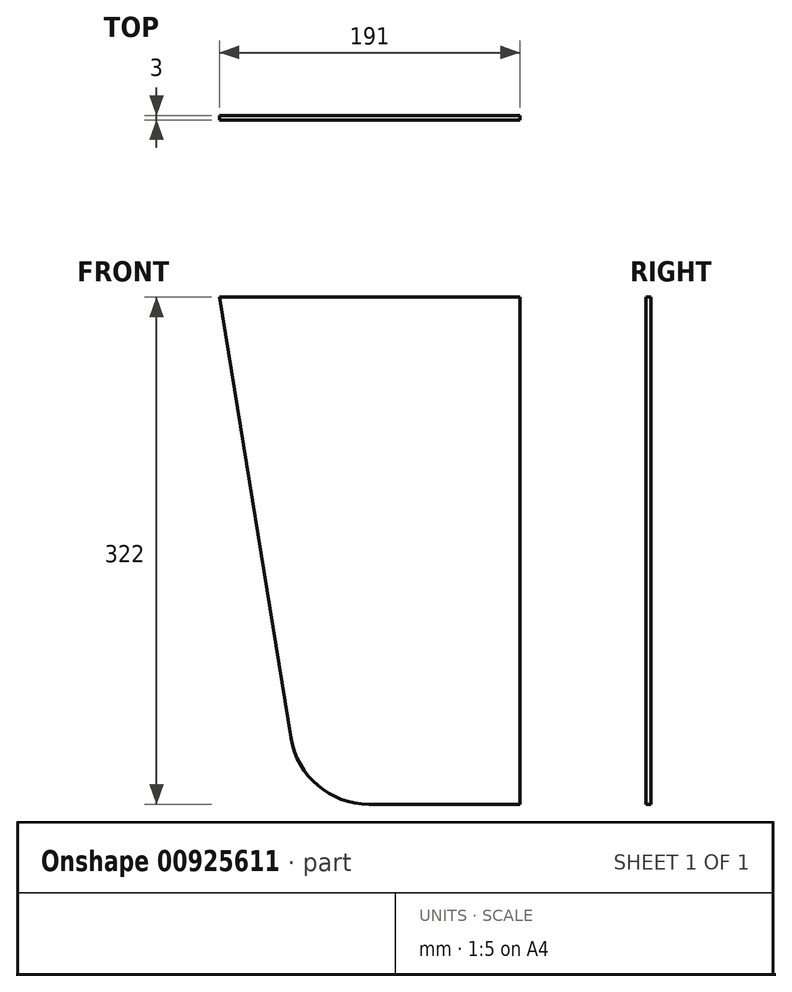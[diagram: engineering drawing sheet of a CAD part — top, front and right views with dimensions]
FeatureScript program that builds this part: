
annotation { "Feature Type Name" : "Feature", "Feature Type Description" : "" }
export const myFeature = defineFeature(function(context is Context, id is Id, definition is map)
    precondition{}
    {
        {
            var Q0;
            Q0=qCreatedBy(makeId("Front.planeOp"),FACE);
            var sketch = newSketch(context, id + "F0", { "sketchPlane" : qUnion([Q0])});
            skLineSegment(sketch, "E0", {"start": v(120.73, -127.8) * mm, "end": v(120.73, 194.2) * mm});
            skLineSegment(sketch, "E1", {"start": v(120.73, 194.2) * mm, "end": v(-70.27, 194.2) * mm});
            skLineSegment(sketch, "E2", {"start": v(-70.27, 194.2) * mm, "end": v(-24.79, -85.81) * mm});
            skLineSegment(sketch, "E3", {"start": v(120.73, -127.8) * mm, "end": v(24.56, -127.8) * mm});
            skPoint(sketch, "E4.visualSharp", {"position": v(-17.97, -127.8) * mm});
            skArc(sketch, "E4.filletArc", {"start": v(-24.79, -85.81) * mm, "mid": v(-7.83, -115.88) * mm, "end": v(24.56, -127.8) * mm});
            skSolve(sketch);
        }
        {
            var Q0;
            Q0=qSketchRegion(id+"F0",true);
            extrude(context, id + "F1", {"entities" : qUnion([Q0]), "depth" : 3 * mm, "offsetDistance" : 25 * mm});
        }
    });
